# Revit family: FP-Revit18-RS7621WRUK1-FridgeFreezer-0-AS-AU-CN-EU-IE-NZ-SG-UK-90001120A
name_source: partatom
category: Specialty Equipment
units: mm (PartAtom-declared; Revit-internal decimal feet)

## family parameters
Always vertical = Yes
Cut with Voids When Loaded = Yes
OmniClass Number = 23.40.40.11.11
OmniClass Title = Refrigerators and Freezers
Part Type = Normal
Room Calculation Point = No
Round Connector Dimension = Use Diameter
Shared = No
Work Plane-Based = No

## types (1)
- RS7621WRUE1
    Cavity - Depth = 650 mm  [stored 2.13255 ft]
    Cavity - Height = 2134 mm  [stored 7.00131 ft]
    Cavity - Width = 762 mm  [stored 2.5 ft]
    Connector Description - Electrical = 230 V, 10 amp fused electrical supply
    Connector Description - Water = 1/2 BSP Stainless steel braided hose
    Default Elevation = 0 mm  [stored 0 ft]
    Description = 76cm Integrated Column Freezer with internal Ice & Water
    Handle Style - Contemporary Round (AHSRD7621W) = No
    Handle Style - Contemporary Square (AHD3RD7621W) = No
    Handle Style - Contemporary Square Fine (AHD5RD7621W) = No
    Handle Style - Contemporary Square Fine Black (AHD5RD7621WB) = No
    Manufacturer = Fisher & Paykel Appliances
    Material - Body = Fisher & Paykel - Grey
    Material - Door Front = Fisher & Paykel - Stainless Steel
    Material - Door Structure = Fisher & Paykel - White
    Material - Handle = Fisher & Paykel - Aluminium, Dark
    Model = RS7621WRUE1
    Product - Depth (exl front panel) = 610 mm  [stored 2.00131 ft]
    Product - Height = 2134 mm  [stored 7.00131 ft]
    Product - Width = 756 mm  [stored 2.48031 ft]
    Stainless Steel Door Panels (RD7621WRD) = No
    URL = www.fisherpaykel.com
    Visibility - Clearance Required = Yes
    Visibility - Visibility Control Note = Yes

note: [stored X ft] marks values corroborated as IEEE doubles in the binary element streams (Revit-internal decimal feet)

## geometry (parser evidence)
native form markers: Sweep x19
no freeform markers — native parametric forms only
